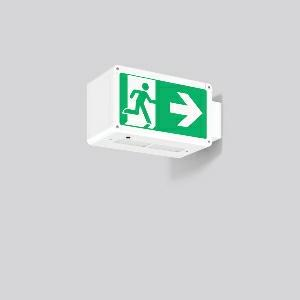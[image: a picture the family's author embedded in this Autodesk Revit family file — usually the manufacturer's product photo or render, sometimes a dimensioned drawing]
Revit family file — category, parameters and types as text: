
# Revit family: rechteck_wandausleger_671049_002_85e7
name_source: partatom
category: Lighting Fixtures
units: mm (PartAtom-declared; Revit-internal decimal feet)

## family parameters
Cut with Voids When Loaded = No
Host = Face
Light Source = No
Part Type = Normal
Room Calculation Point = No
Round Connector Dimension = Use Diameter
Shared = No

## types (1)
- RECHTECK wandausleger
    Apparent Load = 0 VA
    Default Elevation = 1800 mm
    Description = Series: RECHTECK
Rectangular wall extension luminaire in classic design. For escape route identification. Housing: aluminium, with plastic corner connectors. Display panels: plastic, opal, with motifs on one side/on both sides. Wall extension Electronic ballast included. Self-contained system with automatic self-test. Please indicate legend number when placing your order! 
Colour: white
Length: 250 mm
Width: 125 mm
Height: 140 mm
Weight: 1.6 kg
Operating mode: maintained power mode
Viewing Distance: 21 m
Duration time: 3 h
Lamp: LED
Socket: without socket
Colour temperature: 6500K
Colour rendering index (CRI): 70
System power: 6.9 W
Control gear: Regulated power supply
Protection class: I
Type of protection: IP 44
    Height = 140 mm  [stored 0.459318 ft]
    Lamp = 0 x
    Length = 250 mm
    Luminous efficacy = 0 lm/W
    Manufacturer = RZB
    ModVariant = No
    Model = 671049.002
    Mounting Place = Wall
    Mounting Type = Surface mounted
    Number of Poles = 1
    OnlyDefault = Yes
    Power Factor = 1
    Product Name = RECHTECK wandausleger
    Product group = wall cantilever luminaires
    ProductGroupID = 2005
    Protection Class = Protection class I
    Protection Degree = IP 44
    RLX_Detail_Level = 1
    RLX_Emergency_Light_Flux = 0 lm
    RLX_Emergency_Type = 0
    RLX_Emergency_Type_DB = No
    RlxData = <blob elided: 22337 chars, md5=85b728c5>
    Standby Power = 0 W
    System Light Flux = 0 lm
    System Power = 0 W
    Type Comments = Product without accessories
    Type Image = 671049.002.jpg
    URL = http://relux.com
    VarID = ---
    Voltage = 230 V
    Voltage Range = 220-240 V
    Weight = 0.00 kg
    Width = 125 mm

note: [stored X ft] marks values corroborated as IEEE doubles in the binary element streams (Revit-internal decimal feet)

## geometry (parser evidence)
native form markers: Blend x4, Sweep x12
no freeform markers — native parametric forms only
